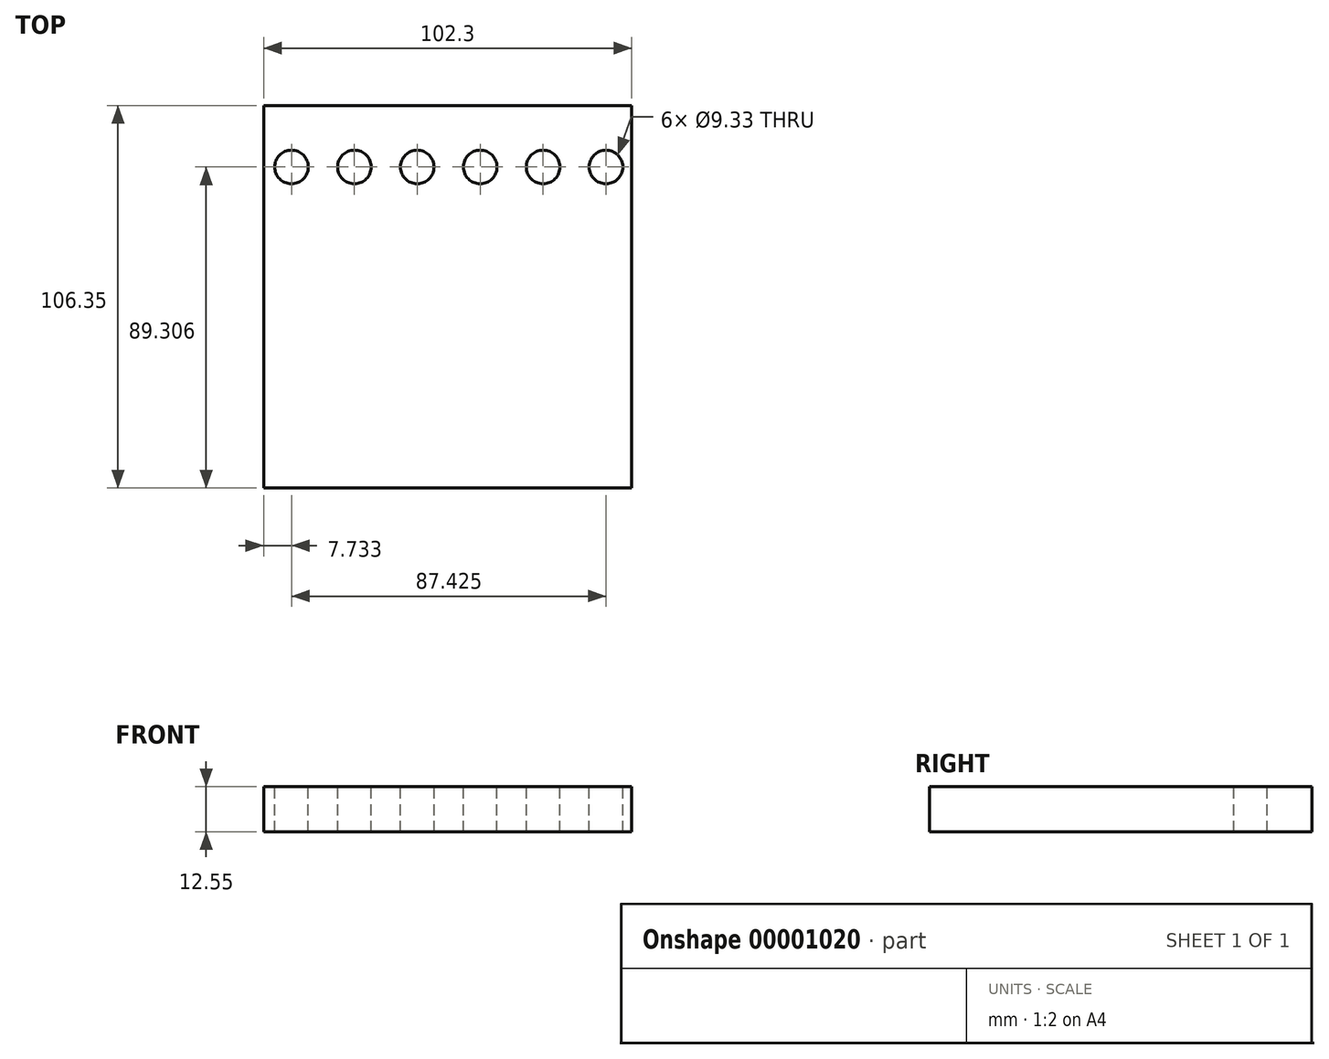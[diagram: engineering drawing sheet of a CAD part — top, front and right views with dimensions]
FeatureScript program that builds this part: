
annotation { "Feature Type Name" : "Feature", "Feature Type Description" : "" }
export const myFeature = defineFeature(function(context is Context, id is Id, definition is map)
    precondition{}
    {
        {
            var Q0;
            Q0=qCreatedBy(makeId("Top.planeOp"),FACE);
            var sketch = newSketch(context, id + "F0", { "sketchPlane" : qUnion([Q0])});
            skLineSegment(sketch, "E0.bottom", {"start": v(-48.02, 48.2) * mm, "end": v(54.28, 48.2) * mm});
            skLineSegment(sketch, "E0.top", {"start": v(-48.02, -58.14) * mm, "end": v(54.28, -58.14) * mm});
            skLineSegment(sketch, "E0.left", {"start": v(-48.02, 48.2) * mm, "end": v(-48.02, -58.14) * mm});
            skLineSegment(sketch, "E0.right", {"start": v(54.28, 48.2) * mm, "end": v(54.28, -58.14) * mm});
            skSolve(sketch);
        }
        {
            var Q0;
            Q0 = qSketchRegion(id + "F0", true);
            extrude(context, id + "F1", {"entities" : qUnion([Q0]), "depth" : 12.55 * mm});
        }
        {
            var Q0;
            Q0=makeQuery(id+"F1.opExtrude","CAP_FACE",FACE,{"disambiguationData":[OSD([sQuery(id+"F0.wireOp",EDGE,"E0.bottom"),sQuery(id+"F0.wireOp",EDGE,"E0.top"),sQuery(id+"F0.wireOp",EDGE,"E0.left"),sQuery(id+"F0.wireOp",EDGE,"E0.right")])],"isStart":false});
            var sketch = newSketch(context, id + "F2", { "sketchPlane" : qUnion([Q0])});
            skCircle(sketch, "E1", {"center": v(-40.29, 31.17) * mm, "radius": 4.67 * mm});
            skCircle(sketch, "E2.1.0.0", {"center": v(-22.8, 31.17) * mm, "radius": 4.67 * mm});
            skCircle(sketch, "E2.2.0.0", {"center": v(-5.32, 31.17) * mm, "radius": 4.67 * mm});
            skCircle(sketch, "E2.3.0.0", {"center": v(12.17, 31.17) * mm, "radius": 4.67 * mm});
            skCircle(sketch, "E2.4.0.0", {"center": v(29.65, 31.17) * mm, "radius": 4.67 * mm});
            skCircle(sketch, "E2.5.0.0", {"center": v(47.14, 31.17) * mm, "radius": 4.67 * mm});
            skLineSegment(sketch, "E2.direction1", {"start": v(-40.29, 31.17) * mm, "end": v(-22.8, 31.17) * mm, "construction": true});
            skSolve(sketch);
        }
        {
            var Q0;
            Q0 = qSketchRegion(id + "F2", true);
            extrude(context, id + "F3", {"entities" : qUnion([Q0]), "operationType" : NewBodyOperationType.REMOVE, "oppositeDirection" : true, "depth" : 25 * mm});
        }
    });
